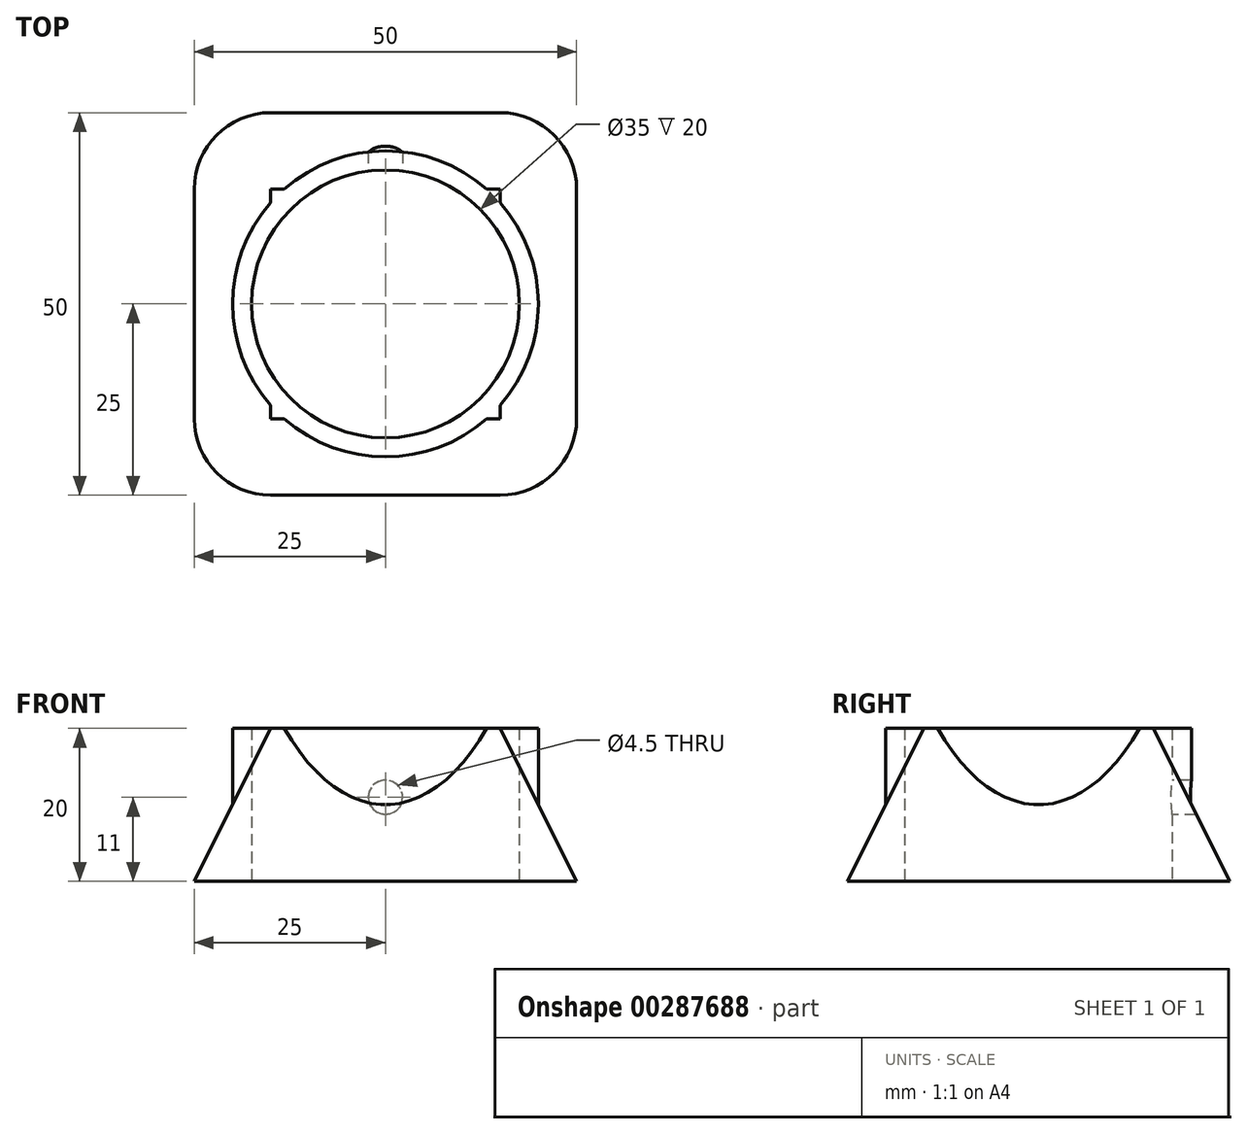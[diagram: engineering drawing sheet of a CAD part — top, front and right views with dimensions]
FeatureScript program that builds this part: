
annotation { "Feature Type Name" : "Feature", "Feature Type Description" : "" }
export const myFeature = defineFeature(function(context is Context, id is Id, definition is map)
    precondition{}
    {
        {
            var Q0;
            Q0=qCreatedBy(makeId("Top.planeOp"),FACE);
            var sketch = newSketch(context, id + "F0", { "sketchPlane" : qUnion([Q0])});
            skCircle(sketch, "E0", {"center": v(0, 0) * mm, "radius": 20 * mm, "construction": true});
            skCircle(sketch, "E1", {"center": v(0, 0) * mm, "radius": 18.5 * mm, "construction": true});
            skCircle(sketch, "E2.cCircle", {"center": v(0, 0) * mm, "radius": 20 * mm});
            skLineSegment(sketch, "E2.0", {"start": v(-20, 0) * mm, "end": v(-19.02, 6.18) * mm, "construction": true});
            skLineSegment(sketch, "E2.1", {"start": v(-19.02, 6.18) * mm, "end": v(-16.18, 11.76) * mm, "construction": true});
            skLineSegment(sketch, "E2.2", {"start": v(-16.18, 11.76) * mm, "end": v(-11.76, 16.18) * mm, "construction": true});
            skLineSegment(sketch, "E2.3", {"start": v(-11.76, 16.18) * mm, "end": v(-6.18, 19.02) * mm, "construction": true});
            skLineSegment(sketch, "E2.4", {"start": v(-6.18, 19.02) * mm, "end": v(0, 20) * mm, "construction": true});
            skLineSegment(sketch, "E2.5", {"start": v(0, 20) * mm, "end": v(6.18, 19.02) * mm, "construction": true});
            skLineSegment(sketch, "E2.6", {"start": v(6.18, 19.02) * mm, "end": v(11.76, 16.18) * mm, "construction": true});
            skLineSegment(sketch, "E2.7", {"start": v(11.76, 16.18) * mm, "end": v(16.18, 11.76) * mm, "construction": true});
            skLineSegment(sketch, "E2.8", {"start": v(16.18, 11.76) * mm, "end": v(19.02, 6.18) * mm, "construction": true});
            skLineSegment(sketch, "E2.9", {"start": v(19.02, 6.18) * mm, "end": v(20, 0) * mm, "construction": true});
            skLineSegment(sketch, "E2.10", {"start": v(20, 0) * mm, "end": v(19.02, -6.18) * mm, "construction": true});
            skLineSegment(sketch, "E2.11", {"start": v(19.02, -6.18) * mm, "end": v(16.18, -11.76) * mm, "construction": true});
            skLineSegment(sketch, "E2.12", {"start": v(16.18, -11.76) * mm, "end": v(11.76, -16.18) * mm, "construction": true});
            skLineSegment(sketch, "E2.13", {"start": v(11.76, -16.18) * mm, "end": v(6.18, -19.02) * mm, "construction": true});
            skLineSegment(sketch, "E2.14", {"start": v(6.18, -19.02) * mm, "end": v(0, -20) * mm, "construction": true});
            skLineSegment(sketch, "E2.15", {"start": v(0, -20) * mm, "end": v(-6.18, -19.02) * mm, "construction": true});
            skLineSegment(sketch, "E2.16", {"start": v(-6.18, -19.02) * mm, "end": v(-11.76, -16.18) * mm, "construction": true});
            skLineSegment(sketch, "E2.17", {"start": v(-11.76, -16.18) * mm, "end": v(-16.18, -11.76) * mm, "construction": true});
            skLineSegment(sketch, "E2.18", {"start": v(-16.18, -11.76) * mm, "end": v(-19.02, -6.18) * mm, "construction": true});
            skLineSegment(sketch, "E2.19", {"start": v(-19.02, -6.18) * mm, "end": v(-20, 0) * mm, "construction": true});
            skLineSegment(sketch, "E3.0", {"start": v(-18.27, -2.9) * mm, "end": v(-18.27, 2.9) * mm, "construction": true});
            skLineSegment(sketch, "E3.1", {"start": v(-18.27, 2.9) * mm, "end": v(-16.48, 8.4) * mm, "construction": true});
            skLineSegment(sketch, "E3.2", {"start": v(-16.48, 8.4) * mm, "end": v(-13.08, 13.08) * mm, "construction": true});
            skLineSegment(sketch, "E3.3", {"start": v(-13.08, 13.08) * mm, "end": v(-8.4, 16.48) * mm, "construction": true});
            skLineSegment(sketch, "E3.4", {"start": v(-8.4, 16.48) * mm, "end": v(-2.9, 18.27) * mm, "construction": true});
            skLineSegment(sketch, "E3.5", {"start": v(-2.9, 18.27) * mm, "end": v(2.9, 18.27) * mm, "construction": true});
            skLineSegment(sketch, "E3.6", {"start": v(2.9, 18.27) * mm, "end": v(8.4, 16.48) * mm, "construction": true});
            skLineSegment(sketch, "E3.7", {"start": v(8.4, 16.48) * mm, "end": v(13.08, 13.08) * mm, "construction": true});
            skLineSegment(sketch, "E3.8", {"start": v(13.08, 13.08) * mm, "end": v(16.48, 8.4) * mm, "construction": true});
            skLineSegment(sketch, "E3.9", {"start": v(16.48, 8.4) * mm, "end": v(18.27, 2.9) * mm, "construction": true});
            skLineSegment(sketch, "E3.10", {"start": v(18.27, 2.9) * mm, "end": v(18.27, -2.9) * mm, "construction": true});
            skLineSegment(sketch, "E3.11", {"start": v(18.27, -2.9) * mm, "end": v(16.48, -8.4) * mm, "construction": true});
            skLineSegment(sketch, "E3.12", {"start": v(16.48, -8.4) * mm, "end": v(13.08, -13.08) * mm, "construction": true});
            skLineSegment(sketch, "E3.13", {"start": v(13.08, -13.08) * mm, "end": v(8.4, -16.48) * mm, "construction": true});
            skLineSegment(sketch, "E3.14", {"start": v(8.4, -16.48) * mm, "end": v(2.9, -18.27) * mm, "construction": true});
            skLineSegment(sketch, "E3.15", {"start": v(2.9, -18.27) * mm, "end": v(-2.9, -18.27) * mm, "construction": true});
            skLineSegment(sketch, "E3.16", {"start": v(-2.9, -18.27) * mm, "end": v(-8.4, -16.48) * mm, "construction": true});
            skLineSegment(sketch, "E3.17", {"start": v(-8.4, -16.48) * mm, "end": v(-13.08, -13.08) * mm, "construction": true});
            skLineSegment(sketch, "E3.18", {"start": v(-13.08, -13.08) * mm, "end": v(-16.48, -8.4) * mm, "construction": true});
            skLineSegment(sketch, "E3.19", {"start": v(-16.48, -8.4) * mm, "end": v(-18.27, -2.9) * mm, "construction": true});
            skLineSegment(sketch, "E4", {"start": v(-18.27, 2.9) * mm, "end": v(-19.02, 6.18) * mm, "construction": true});
            skLineSegment(sketch, "E5", {"start": v(-16.48, 8.4) * mm, "end": v(-19.02, 6.18) * mm, "construction": true});
            skLineSegment(sketch, "E6", {"start": v(-16.18, 11.76) * mm, "end": v(-16.48, 8.4) * mm, "construction": true});
            skLineSegment(sketch, "E7", {"start": v(-13.08, 13.08) * mm, "end": v(-16.18, 11.76) * mm, "construction": true});
            skLineSegment(sketch, "E8", {"start": v(-13.08, 13.08) * mm, "end": v(-11.76, 16.18) * mm, "construction": true});
            skLineSegment(sketch, "E9", {"start": v(-11.76, 16.18) * mm, "end": v(-8.4, 16.48) * mm, "construction": true});
            skLineSegment(sketch, "E10", {"start": v(-8.4, 16.48) * mm, "end": v(-6.18, 19.02) * mm, "construction": true});
            skLineSegment(sketch, "E11", {"start": v(-6.18, 19.02) * mm, "end": v(-2.9, 18.27) * mm, "construction": true});
            skLineSegment(sketch, "E12", {"start": v(-2.9, 18.27) * mm, "end": v(0, 20) * mm, "construction": true});
            skLineSegment(sketch, "E13", {"start": v(2.9, 18.27) * mm, "end": v(0, 20) * mm, "construction": true});
            skLineSegment(sketch, "E14", {"start": v(2.9, 18.27) * mm, "end": v(6.18, 19.02) * mm, "construction": true});
            skLineSegment(sketch, "E15", {"start": v(8.4, 16.48) * mm, "end": v(6.18, 19.02) * mm, "construction": true});
            skLineSegment(sketch, "E16", {"start": v(8.4, 16.48) * mm, "end": v(11.76, 16.18) * mm, "construction": true});
            skLineSegment(sketch, "E17", {"start": v(11.76, 16.18) * mm, "end": v(13.08, 13.08) * mm, "construction": true});
            skLineSegment(sketch, "E18", {"start": v(16.18, 11.76) * mm, "end": v(13.08, 13.08) * mm, "construction": true});
            skLineSegment(sketch, "E19", {"start": v(16.18, 11.76) * mm, "end": v(16.48, 8.4) * mm, "construction": true});
            skLineSegment(sketch, "E20", {"start": v(19.02, 6.18) * mm, "end": v(16.48, 8.4) * mm, "construction": true});
            skLineSegment(sketch, "E21", {"start": v(18.27, 2.9) * mm, "end": v(20, 0) * mm, "construction": true});
            skLineSegment(sketch, "E22", {"start": v(18.27, 2.9) * mm, "end": v(19.02, 6.18) * mm, "construction": true});
            skLineSegment(sketch, "E23", {"start": v(20, 0) * mm, "end": v(18.27, -2.9) * mm, "construction": true});
            skLineSegment(sketch, "E24", {"start": v(19.02, -6.18) * mm, "end": v(18.27, -2.9) * mm, "construction": true});
            skLineSegment(sketch, "E25", {"start": v(16.48, -8.4) * mm, "end": v(19.02, -6.18) * mm, "construction": true});
            skLineSegment(sketch, "E26", {"start": v(16.18, -11.76) * mm, "end": v(16.48, -8.4) * mm, "construction": true});
            skLineSegment(sketch, "E27", {"start": v(16.18, -11.76) * mm, "end": v(13.08, -13.08) * mm, "construction": true});
            skLineSegment(sketch, "E28", {"start": v(13.08, -13.08) * mm, "end": v(11.76, -16.18) * mm, "construction": true});
            skLineSegment(sketch, "E29", {"start": v(11.76, -16.18) * mm, "end": v(8.4, -16.48) * mm, "construction": true});
            skLineSegment(sketch, "E30", {"start": v(8.4, -16.48) * mm, "end": v(6.18, -19.02) * mm, "construction": true});
            skLineSegment(sketch, "E31", {"start": v(6.18, -19.02) * mm, "end": v(2.9, -18.27) * mm, "construction": true});
            skLineSegment(sketch, "E32", {"start": v(2.9, -18.27) * mm, "end": v(0, -20) * mm, "construction": true});
            skLineSegment(sketch, "E33", {"start": v(0, -20) * mm, "end": v(-2.9, -18.27) * mm, "construction": true});
            skLineSegment(sketch, "E34", {"start": v(-2.9, -18.27) * mm, "end": v(-6.18, -19.02) * mm, "construction": true});
            skLineSegment(sketch, "E35", {"start": v(-8.4, -16.48) * mm, "end": v(-6.18, -19.02) * mm, "construction": true});
            skLineSegment(sketch, "E36", {"start": v(-8.4, -16.48) * mm, "end": v(-11.76, -16.18) * mm, "construction": true});
            skLineSegment(sketch, "E37", {"start": v(-13.08, -13.08) * mm, "end": v(-11.76, -16.18) * mm, "construction": true});
            skLineSegment(sketch, "E38", {"start": v(-16.18, -11.76) * mm, "end": v(-13.08, -13.08) * mm, "construction": true});
            skLineSegment(sketch, "E39", {"start": v(-16.18, -11.76) * mm, "end": v(-16.48, -8.4) * mm, "construction": true});
            skLineSegment(sketch, "E40", {"start": v(-19.02, -6.18) * mm, "end": v(-16.48, -8.4) * mm, "construction": true});
            skLineSegment(sketch, "E41", {"start": v(-19.02, -6.18) * mm, "end": v(-18.27, -2.9) * mm, "construction": true});
            skLineSegment(sketch, "E42", {"start": v(-18.27, -2.9) * mm, "end": v(-20, 0) * mm, "construction": true});
            skLineSegment(sketch, "E43", {"start": v(-20, 0) * mm, "end": v(-18.27, 2.9) * mm, "construction": true});
            skCircle(sketch, "E44", {"center": v(0, 0) * mm, "radius": 17.5 * mm});
            skCircle(sketch, "E45", {"center": v(0, 0) * mm, "radius": 19.5 * mm, "construction": true});
            skLineSegment(sketch, "E46.bottom", {"start": v(-11.36, 15.85) * mm, "end": v(11.36, 15.85) * mm, "construction": true});
            skLineSegment(sketch, "E46.top", {"start": v(-11.36, -15.85) * mm, "end": v(11.36, -15.85) * mm, "construction": true});
            skLineSegment(sketch, "E46.left", {"start": v(-11.36, 15.85) * mm, "end": v(-11.36, -15.85) * mm, "construction": true});
            skLineSegment(sketch, "E46.right", {"start": v(11.36, 15.85) * mm, "end": v(11.36, -15.85) * mm, "construction": true});
            skLineSegment(sketch, "E47.bottom", {"start": v(-2.5, 19.34) * mm, "end": v(2.5, 19.34) * mm, "construction": true});
            skLineSegment(sketch, "E47.top", {"start": v(-2.5, -19.34) * mm, "end": v(2.5, -19.34) * mm, "construction": true});
            skLineSegment(sketch, "E47.left", {"start": v(-2.5, 19.34) * mm, "end": v(-2.5, -19.34) * mm, "construction": true});
            skLineSegment(sketch, "E47.right", {"start": v(2.5, 19.34) * mm, "end": v(2.5, -19.34) * mm, "construction": true});
            skLineSegment(sketch, "E48.bottom", {"start": v(-19.42, 1.75) * mm, "end": v(19.42, 1.75) * mm, "construction": true});
            skLineSegment(sketch, "E48.top", {"start": v(-19.42, -1.75) * mm, "end": v(19.42, -1.75) * mm, "construction": true});
            skLineSegment(sketch, "E48.left", {"start": v(-19.42, 1.75) * mm, "end": v(-19.42, -1.75) * mm, "construction": true});
            skLineSegment(sketch, "E48.right", {"start": v(19.42, 1.75) * mm, "end": v(19.42, -1.75) * mm, "construction": true});
            skLineSegment(sketch, "E49.bottom", {"start": v(-14.42, 1.75) * mm, "end": v(14.42, 1.75) * mm, "construction": true});
            skLineSegment(sketch, "E49.top", {"start": v(-14.42, -1.75) * mm, "end": v(14.42, -1.75) * mm, "construction": true});
            skLineSegment(sketch, "E49.left", {"start": v(-14.42, 1.75) * mm, "end": v(-14.42, -1.75) * mm, "construction": true});
            skLineSegment(sketch, "E49.right", {"start": v(14.42, 1.75) * mm, "end": v(14.42, -1.75) * mm, "construction": true});
            skCircle(sketch, "E50", {"center": v(0, 0) * mm, "radius": 18 * mm, "construction": true});
            skLineSegment(sketch, "E51.bottom", {"start": v(10.87, 14.35) * mm, "end": v(-10.87, 14.35) * mm, "construction": true});
            skLineSegment(sketch, "E51.top", {"start": v(10.87, -14.35) * mm, "end": v(-10.87, -14.35) * mm, "construction": true});
            skLineSegment(sketch, "E51.left", {"start": v(10.87, 14.35) * mm, "end": v(10.87, -14.35) * mm, "construction": true});
            skLineSegment(sketch, "E51.right", {"start": v(-10.87, 14.35) * mm, "end": v(-10.87, -14.35) * mm, "construction": true});
            skLineSegment(sketch, "E52.bottom", {"start": v(-12.92, 12.53) * mm, "end": v(12.92, 12.53) * mm, "construction": true});
            skLineSegment(sketch, "E52.top", {"start": v(-12.92, -12.53) * mm, "end": v(12.92, -12.53) * mm, "construction": true});
            skLineSegment(sketch, "E52.left", {"start": v(-12.92, 12.53) * mm, "end": v(-12.92, -12.53) * mm, "construction": true});
            skLineSegment(sketch, "E52.right", {"start": v(12.92, 12.53) * mm, "end": v(12.92, -12.53) * mm, "construction": true});
            skLineSegment(sketch, "E53.bottom", {"start": v(15, 25) * mm, "end": v(-15, 25) * mm});
            skLineSegment(sketch, "E53.top", {"start": v(15, -25) * mm, "end": v(-15, -25) * mm});
            skLineSegment(sketch, "E53.left", {"start": v(25, 15) * mm, "end": v(25, -15) * mm});
            skLineSegment(sketch, "E53.right", {"start": v(-25, 15) * mm, "end": v(-25, -15) * mm});
            skPoint(sketch, "E54.visualSharp", {"position": v(25, 25) * mm});
            skArc(sketch, "E54.filletArc", {"start": v(25, 15) * mm, "mid": v(22.07, 22.07) * mm, "end": v(15, 25) * mm});
            skPoint(sketch, "E55.visualSharp", {"position": v(-25, 25) * mm});
            skArc(sketch, "E55.filletArc", {"start": v(-15, 25) * mm, "mid": v(-22.07, 22.07) * mm, "end": v(-25, 15) * mm});
            skPoint(sketch, "E56.visualSharp", {"position": v(25, -25) * mm});
            skArc(sketch, "E56.filletArc", {"start": v(15, -25) * mm, "mid": v(22.07, -22.07) * mm, "end": v(25, -15) * mm});
            skPoint(sketch, "E57.visualSharp", {"position": v(-25, -25) * mm});
            skArc(sketch, "E57.filletArc", {"start": v(-25, -15) * mm, "mid": v(-22.07, -22.07) * mm, "end": v(-15, -25) * mm});
            skSolve(sketch);
        }
        {
            var Q0;
            Q0=makeQuery(id+"F0.imprint","IMPRINT",FACE,{"disambiguationData":[TD([[makeQuery(id+"F0.imprint","IMPRINT",EDGE,{"derivedFrom":sQuery(id+"F0.wireOp",EDGE,"E53.bottom")}),1.0]])]});
            extrude(context, id + "F1", {"entities" : qUnion([Q0]), "depth" : 20 * mm, "offsetDistance" : 25 * mm});
        }
        {
            var Q0;
            Q0=makeQuery(id+"F1.opExtrude","CAP_EDGE",EDGE,{"disambiguationData":[OSD([sQuery(id+"F0.wireOp",EDGE,"E53.top")])],"isStart":false});
            chamfer(context, id + "F2", {"entities" : qUnion([Q0]), "chamferType" : ChamferType.TWO_OFFSETS, "width1" : 20 * mm, "oppositeDirection" : false, "width2" : 10 * mm, "tangentPropagation" : true});
        }
        {
            var Q0;
            Q0=makeQuery(id+"F0.imprint","IMPRINT",FACE,{"disambiguationData":[TD([[makeQuery(id+"F0.imprint","IMPRINT",EDGE,{"derivedFrom":sQuery(id+"F0.wireOp",EDGE,"E2.cCircle")}),1.0]])]});
            extrude(context, id + "F3", {"entities" : qUnion([Q0]), "operationType" : NewBodyOperationType.ADD, "depth" : 20 * mm, "offsetDistance" : 25 * mm});
        }
        {
            var Q0;
            Q0=qCreatedBy(makeId("Front.planeOp"),FACE);
            var sketch = newSketch(context, id + "F4", { "sketchPlane" : qUnion([Q0])});
            skCircle(sketch, "E58", {"center": v(0, 11) * mm, "radius": 2.25 * mm});
            skSolve(sketch);
        }
        {
            var Q0;
            Q0=makeQuery(id+"F4.imprint","IMPRINT",FACE,{"disambiguationData":[TD([[makeQuery(id+"F4.imprint","IMPRINT",EDGE,{"derivedFrom":sQuery(id+"F4.wireOp",EDGE,"E58")}),1.0]])]});
            extrude(context, id + "F5", {"entities" : qUnion([Q0]), "operationType" : NewBodyOperationType.REMOVE, "oppositeDirection" : true, "depth" : 25 * mm, "offsetDistance" : 25 * mm});
        }
    });
